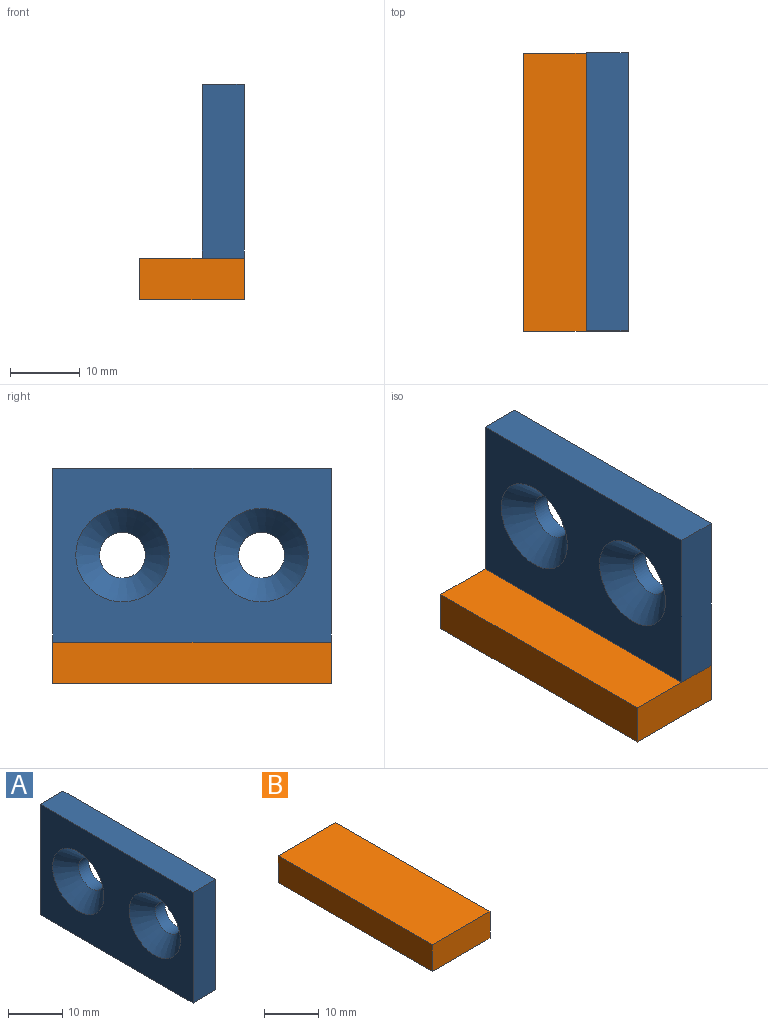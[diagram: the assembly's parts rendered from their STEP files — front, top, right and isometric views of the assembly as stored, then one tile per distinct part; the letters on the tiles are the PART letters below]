
ASSEMBLY  parts=2 mates=1
PART A: 10 faces, bbox 6x40x25 mm
  f0: plane 25x6mm, normal (0,1,0), area 150mm2, adj f1,f3,f4,f5
  f1: plane 40x25mm, normal (-1,0,0), area 716.3mm2, adj f0,f2,f4,f5,f7,f9
  f2: plane 25x6mm, normal (0,-1,0), area 150mm2, adj f1,f3,f4,f5
  f3: plane 40x25mm, normal (1,0,0), area 931.6mm2, adj f0,f2,f4,f5,f6,f8
  f4: plane 40x6mm, normal (0,0,1), area 240mm2, adj f0,f1,f2,f3
  f5: plane 40x6mm, normal (0,0,-1), area 240mm2, adj f0,f1,f2,f3
  f6: cylinder r=3.3mm len=6.6mm, axis (-1,0,0), area 53.5mm2, adj f3,f7
  f7: cone r=3.3mm half-angle=45deg, axis (-1,0,0), area 152.3mm2, adj f1,f6
  f8: cylinder r=3.3mm len=6.6mm, axis (-1,0,0), area 53.5mm2, adj f3,f9
  f9: cone r=3.3mm half-angle=45deg, axis (-1,0,0), area 152.3mm2, adj f1,f8
PART B: 6 faces, bbox 15x40x6 mm
  f0: plane 40x15mm, normal (0,0,1), area 600mm2, adj f1,f3,f4,f5
  f1: plane 15x6mm, normal (0,-1,0), area 90mm2, adj f0,f2,f4,f5
  f2: plane 40x15mm, normal (0,0,-1), area 600mm2, adj f1,f3,f4,f5
  f3: plane 15x6mm, normal (0,1,0), area 90mm2, adj f0,f2,f4,f5
  f4: plane 40x6mm, normal (1,0,0), area 240mm2, adj f0,f1,f2,f3
  f5: plane 40x6mm, normal (-1,0,0), area 240mm2, adj f0,f1,f2,f3
PLACE A t=(-4.54,0,0)mm fixed
PLACE B t=(-4.54,0,0)mm
MATE fastened B.f0 <-> A.f5  axis (0,0,1) through (50.46,-234,2000)mm
